# Revit family: TataSteel_Lintels_CX_150-165_100-115
name_source: partatom
category: Generic Models
revit_build: Autodesk Revit 2015 (Build: 20140606_1530(x64)
units: mm (PartAtom-declared; Revit-internal decimal feet)

## types (1)
- TataSteel_Lintels_CX_150-165_100-115
    AllowableLoadLimiting = 74 mm  [stored 0.242782 ft]
    AssetType = FIXED
    BIMObjectName = TataSteel_Lintel_CXC150_100_2550
    BIMobject category = Beams & Lintels
    CharacteristicDeflectionUnderLoad = 0 mm  [stored 0 ft]
    CharacteristicResistanceToFire = 60 mm  [stored 0.19685 ft]
    CharacteristicThermalConductivity = 0 mm  [stored 0 ft]
    Color = Black
    Date of publishing = 7/15/2016
    Description = Extra heavy duty cavity wall lintel
    Edition number = 1
    ExpectedLife = 60 yrs
    Finish = Galv and Powder coated
    FireRating = 60
    Grade = DX51
    IFC Classification = Structural Member
    IfcExportAs = IfcBeamType
    IfcExportType = LINTEL
    Installation instructions = http://catnic.com
    InstallationDate = 1900-12-31T23:59:59
    Insulation = Steel
    IsExternal = Yes
    LengthIncrement = 150mm up to 3000mm. 
300mm above 3000mm
    LintelCavity = 148 mm  [stored 0.485564 ft]
    LintelHeight = 233 mm  [stored 0.764436 ft]
    LintelInnerLeaf = 100 mm  [stored 0.328084 ft]
    LintelLength = 2550 mm  [stored 8.36614 ft]
    LintelOuterLeaf = 95 mm
    LintelPlateThickness = 2 mm  [stored 0.00656168 ft]
    LintelPlateWidth = 216 mm  [stored 0.708661 ft]
    LintelThickness = 3 mm  [stored 0.00984252 ft]
    LintelTopFlange1 = 53 mm  [stored 0.173885 ft]
    LintelTopFlange2 = 48 mm  [stored 0.15748 ft]
    LintelType = CAVITY
    LoadBearing = Yes
    LoadCategory = EXTRA HEAVY DUTY
    Manufacturer = Catnic, TATA
    Manufacturer country = United Kingdom
    Manufacturer name = Tata Steel
    ManufacturerURL = www.catnic.com
    Material = Galvanised Steel
    Material main = Steel
    MaxLintelLength = 4800
    MinLintelLength = 900
    Model = TataSteel_Lintel_CXC150_100_2550
    ModelNumber = CX
    ModelReference = Cavity Walls
    NBSDescription = Pre fabricated Steel Lintel
    NBSReference = F30 755
    Name = Lintel
    Nominal height = 0
    Nominal width = 0
    NominalLength = 2550 mm  [stored 8.36614 ft]
    OmniClass Code = 23-13 21 25 11
    OmniClass Description = Lintels
    Product Guid = 841d2093-a710-46a7-8c81-f3d746250bcf
    Product SKU = catnic-cx
    Product certification = http://catnic.com
    Product family = Lintels
    Product group = Catnic
    ProductInformation = www.catnic.com
    QR code = http://bimobject.com
    Roll = 0 mm  [stored 0 ft]
    SafeWorkingLoad = 74 mm  [stored 0.242782 ft]
    Shape = Open back lintel
    Size = 233H x350W x2550L
    Slope = 0 mm  [stored 0 ft]
    Span = 2250 mm
    Steel = Steel
    TSE_BIMObjectName = TataSteel_Lintel_CXC150_100_2550
    TSE_Documentation = www.catnic.com
    TSE_InstallationInstructions = www.catnic.com
    TSE_ManufacturerURL = www.catnic.com
    TSE_Model = TataSteel_Lintel_CXC150_100_2550
    TSE_ProductCertification = www.catnic.com
    TSE_QR code = <None>
    Technical description = http://catnic.com
    ThermalTransmittance = 0 mm  [stored 0 ft]
    UNSPSC Code = 30101704
    URL = www.catnic.com
    Uniclass 1.4 Code = L3241
    Uniclass 1.4 Description = Lintels
    Uniclass 2015 Code = Pr_20_85_48
    Uniclass 2015 Name = Lintels
    Uniclass2015 = Pr_20_85_48_11
    WallCavityRange = 150-165
    WallInnerLeafRange = 100-115
    WarrantyStartDate = 1900-12-31T23:59:59
    Weight = 22 mm
    Weight Net (Kg) = 0
    b1 = 169 mm
    b2 = 174 mm  [stored 0.570866 ft]
    b3 = 74 mm  [stored 0.242782 ft]
    b5 = 2 mm  [stored 0.00656168 ft]
    b6 = 108 mm  [stored 0.354331 ft]

note: [stored X ft] marks values corroborated as IEEE doubles in the binary element streams (Revit-internal decimal feet)

## geometry (parser evidence)
native form markers: Sweep x3
no freeform markers — native parametric forms only
